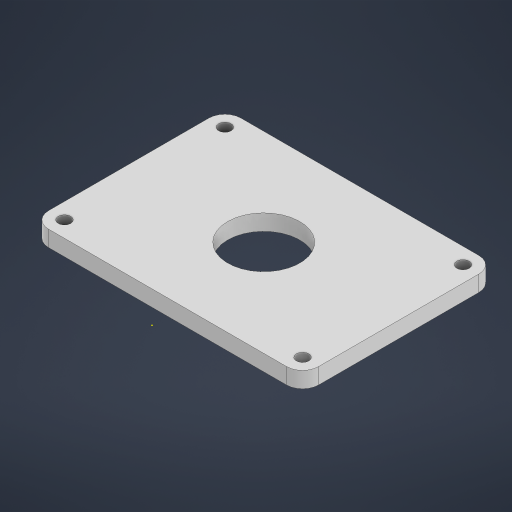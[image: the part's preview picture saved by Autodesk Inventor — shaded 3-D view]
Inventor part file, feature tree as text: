
AUTODESK INVENTOR PART (.ipt)
format: ipt  version: 2024.3 (Build 283343000, 343)  size: 210,944 bytes
history: native  units: in
note: dims shown in document units (in); Inventor stores cm internally (conversion verified against a paired STEP export)
features: sketch x2, extrude x1
ambient origin geometry x8: Origin, YZ Plane, XZ Plane, XY Plane, X Axis, Y Axis, Z Axis, Center Point
bodies: Body1 (feature_tree)
feature tree (3):
  sketch  "Sketch1"  dims[d0=0.5in d1=3.0in]
  extrude  "Extrusion2"  Depth=3.0in
  sketch  "Sketch2"  dims[d2=2.0in d3=0.196in d4=3.1496in d6=360.0deg d8=0.196in d9=3.1496in d11=360.0deg d13=0.75in d14=0.75in d15=2.36in d16=2.36in d17=0.5in d18=0.196in d24=0.5in d25=1.13in d30=0.25in d31=0.0in]
